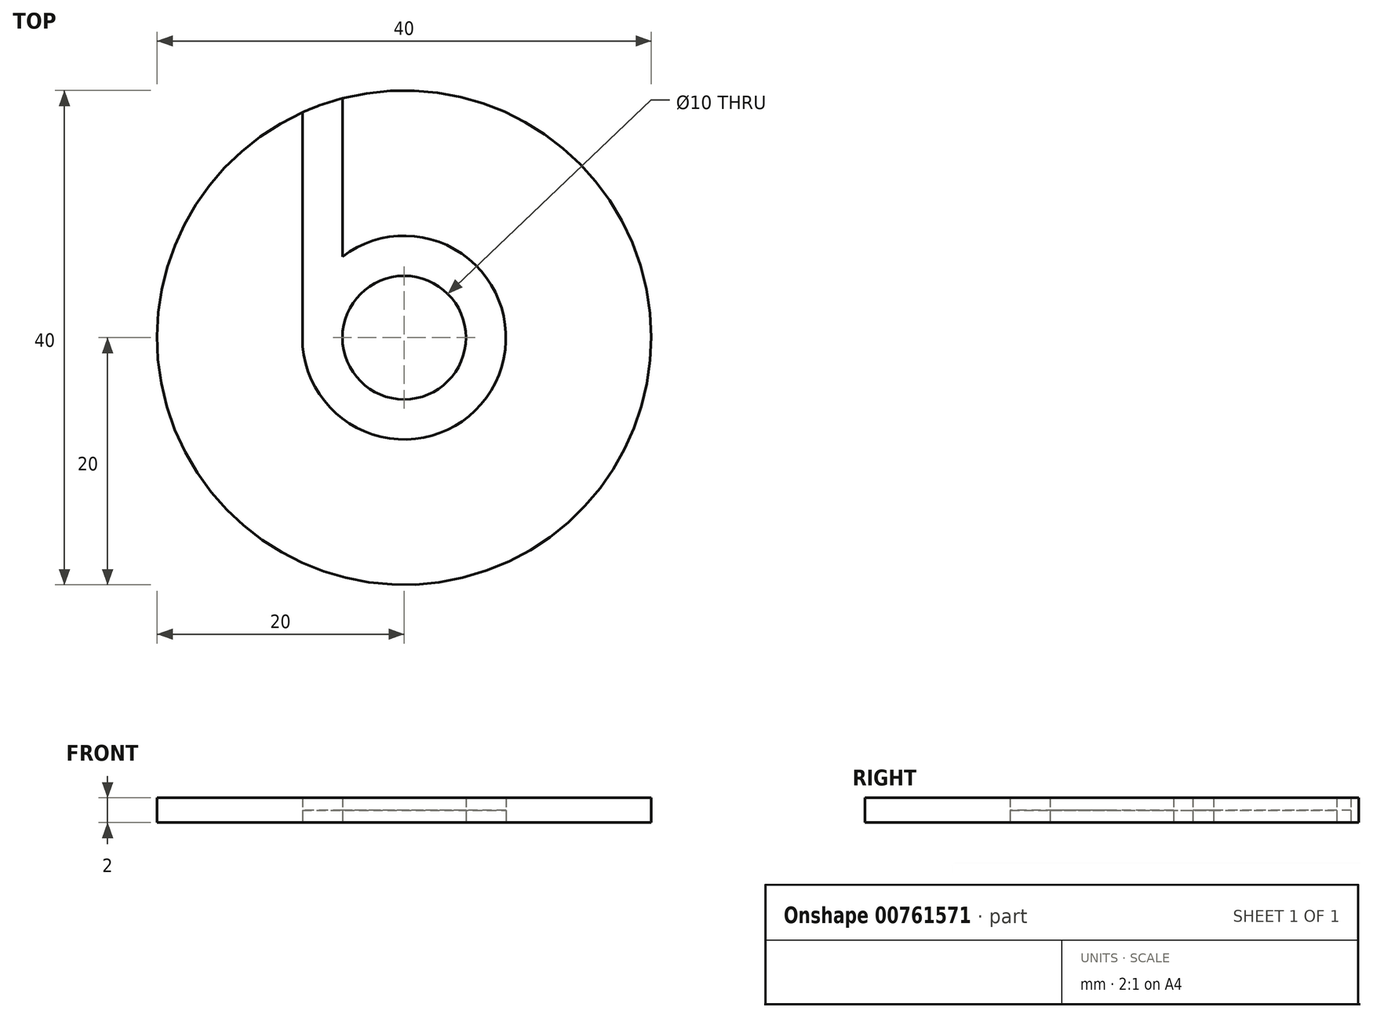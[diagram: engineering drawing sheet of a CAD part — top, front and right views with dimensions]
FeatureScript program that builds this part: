
annotation { "Feature Type Name" : "Feature", "Feature Type Description" : "" }
export const myFeature = defineFeature(function(context is Context, id is Id, definition is map)
    precondition{}
    {
        {
            var Q0;
            Q0=qCreatedBy(makeId("Top.planeOp"),FACE);
            var sketch = newSketch(context, id + "F0", { "sketchPlane" : qUnion([Q0])});
            skCircle(sketch, "E0", {"center": v(0, 0) * mm, "radius": 20 * mm});
            skCircle(sketch, "E1", {"center": v(0, 0) * mm, "radius": 5 * mm});
            skLineSegment(sketch, "E2", {"start": v(-5, 19.36) * mm, "end": v(-5, 6.55) * mm});
            skLineSegment(sketch, "E3", {"start": v(-8.24, 0) * mm, "end": v(-8.24, 18.22) * mm});
            skArc(sketch, "E4", {"start": v(-8.24, 0) * mm, "mid": v(7.39, -3.65) * mm, "end": v(-5, 6.55) * mm});
            skSolve(sketch);
        }
        {
            var Q0;
            {var subQ0=sQuery(id+"F0.wireOp",EDGE,"E2");Q0=makeQuery(id+"F0.imprint","IMPRINT",FACE,{"disambiguationData":[TD([[makeQuery(id+"F0.imprint","IMPRINT",EDGE,{"derivedFrom":subQ0}),1.0]])]});}
            var Q1;
            Q1=makeQuery(id+"F0.imprint","IMPRINT",FACE,{"disambiguationData":[TD([[makeQuery(id+"F0.imprint","IMPRINT",EDGE,{"derivedFrom":sQuery(id+"F0.wireOp",EDGE,"E1")}),1.0]])]});
            extrude(context, id + "F1", {"entities" : qUnion([Q0, Q1]), "depth" : 2 * mm, "offsetDistance" : 25 * mm});
        }
        {
            var Q0;
            Q0=makeQuery(id+"F0.imprint","IMPRINT",FACE,{"disambiguationData":[TD([[makeQuery(id+"F0.imprint","IMPRINT",EDGE,{"derivedFrom":sQuery(id+"F0.wireOp",EDGE,"E1")}),-1.0]])]});
            extrude(context, id + "F2", {"entities" : qUnion([Q0]), "depth" : 1 * mm, "offsetDistance" : 25 * mm});
        }
    });
